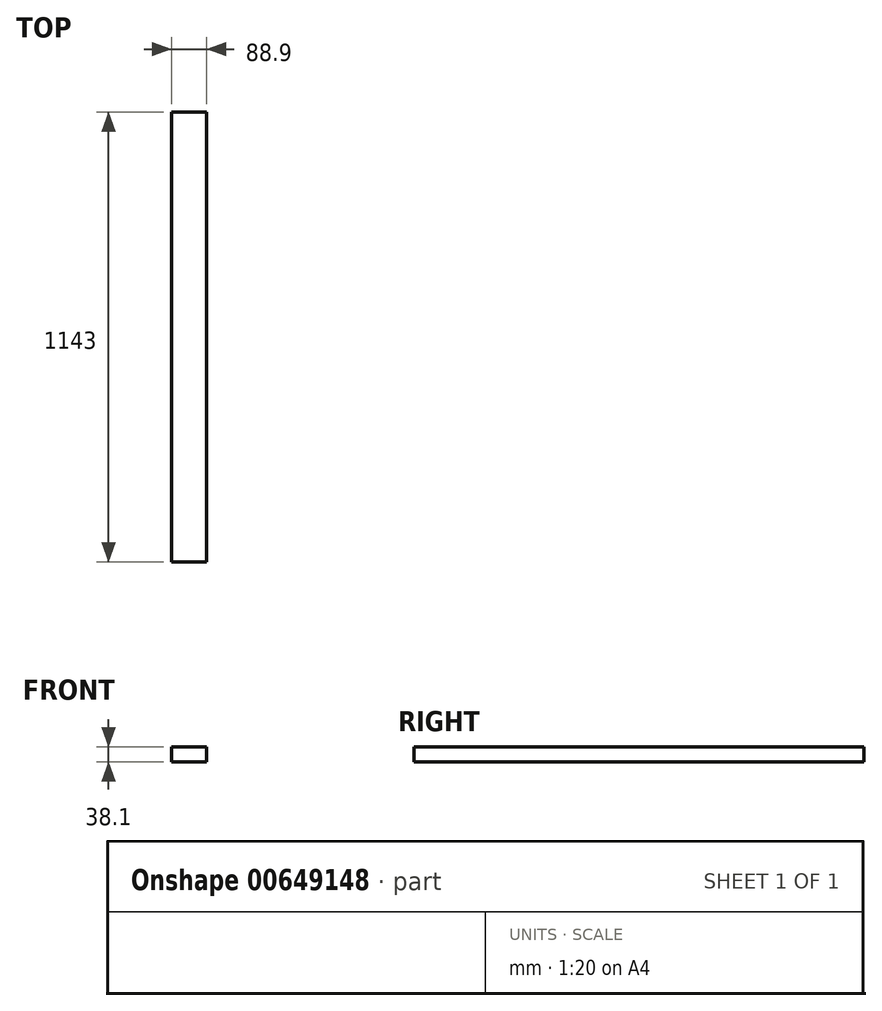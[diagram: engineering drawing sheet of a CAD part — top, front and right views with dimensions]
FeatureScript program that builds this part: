
annotation { "Feature Type Name" : "Feature", "Feature Type Description" : "" }
export const myFeature = defineFeature(function(context is Context, id is Id, definition is map)
    precondition{}
    {
        {
            var Q0;
            Q0=qCreatedBy(makeId("Front.planeOp"),FACE);
            var sketch = newSketch(context, id + "F0", { "sketchPlane" : qUnion([Q0])});
            skLineSegment(sketch, "E0.bottom", {"start": v(0, 0) * mm, "end": v(88.9, 0) * mm});
            skLineSegment(sketch, "E0.top", {"start": v(0, 38.1) * mm, "end": v(88.9, 38.1) * mm});
            skLineSegment(sketch, "E0.left", {"start": v(0, 0) * mm, "end": v(0, 38.1) * mm});
            skLineSegment(sketch, "E0.right", {"start": v(88.9, 0) * mm, "end": v(88.9, 38.1) * mm});
            skSolve(sketch);
        }
        {
            var Q0;
            Q0=qSketchRegion(id+"F0",true);
            extrude(context, id + "F1", {"entities" : qUnion([Q0]), "depth" : 1143 * mm, "offsetDistance" : 25.4 * mm});
        }
    });
